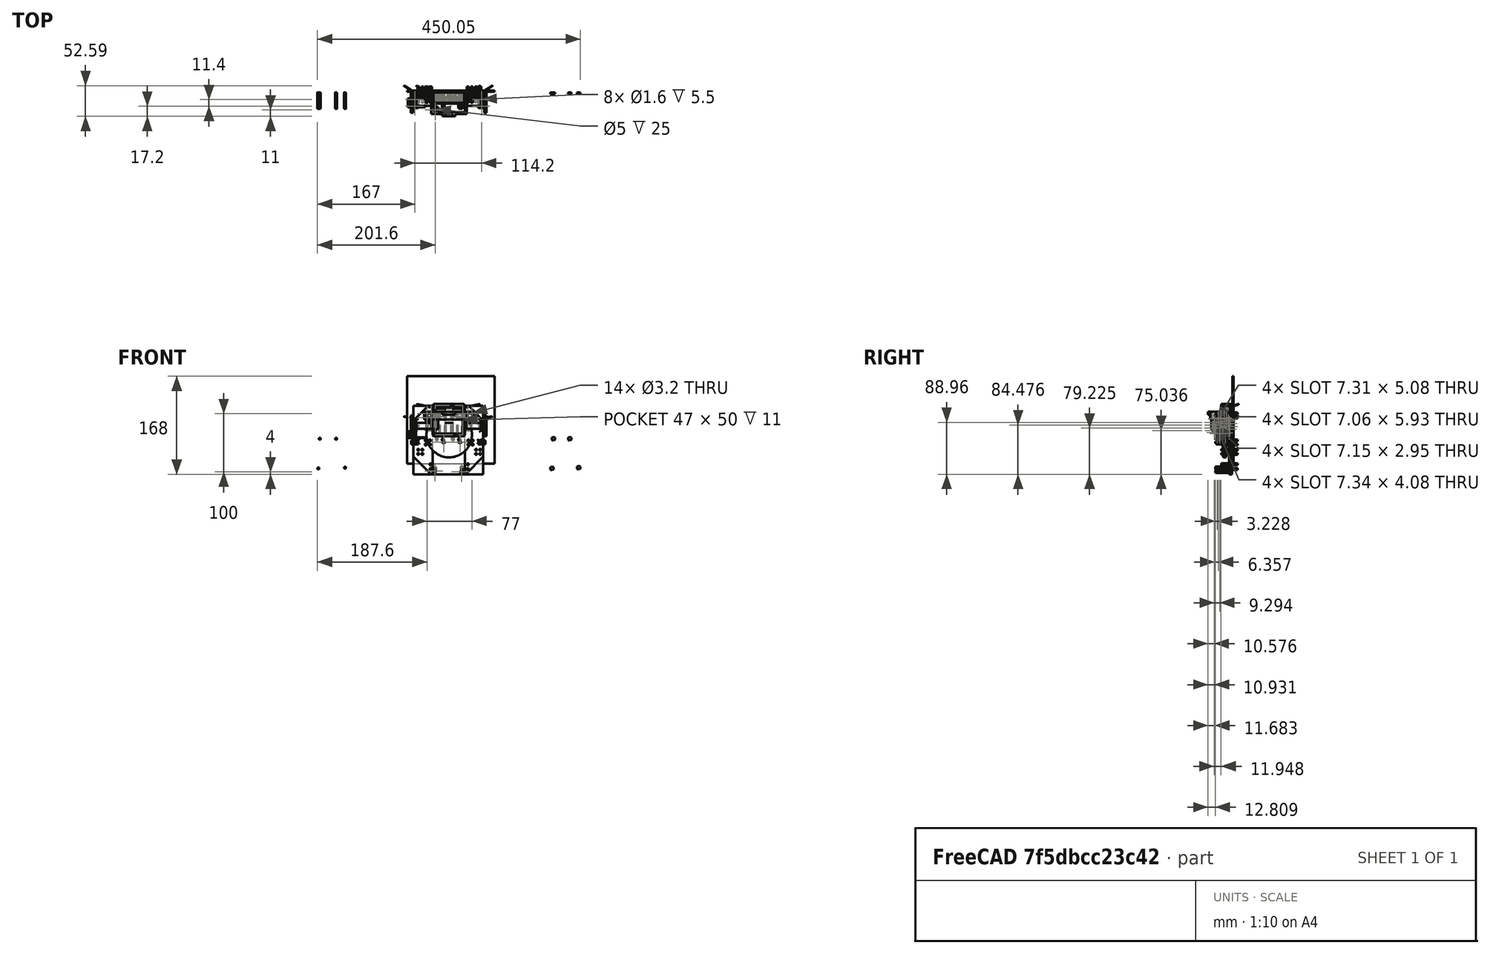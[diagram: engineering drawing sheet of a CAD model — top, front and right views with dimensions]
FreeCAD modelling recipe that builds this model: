
FCSTD DOCUMENT  (FreeCAD 0.16R6712 (Git))
Label: 5028.4 Blank Frank
License: All rights reserved
LicenseURL: http://en.wikipedia.org/wiki/All_rights_reserved
objects: Part::Cylinder×127, Part::Box×74, Part::Fuse×65, Part::Cut×64, Part::Feature×37, Part::MultiFuse×31, Part::Mirroring×14, Part::Fillet×10, Part::Chamfer×8, Part::Cone×8, Part::Compound×3, Part::Torus×2, App::DocumentObjectGroup×1
note: 443 computed .brp shape members not serialized (recipe doc carries the construction recipe); baked Part::Feature solids carry a one-line shape summary decoded from their .brp

FEATURE [Part::Cylinder] Cylinder
  Angle = 360
  Height = 30
  Radius = 7
FEATURE [Part::Cylinder] Cylinder001
  Angle = 360
  Height = 19
  Placement = pos=(0,0,30) rot=(0,0,1;0rad)
  Radius = 7
FEATURE [Part::Cylinder] Cylinder002
  Angle = 360
  Height = 1.8
  Placement = pos=(0,0,49) rot=(0,0,1;0rad)
  Radius = 2.5
FEATURE [Part::Compound] Compound
  Links = -> [Cylinder,Cylinder002,Cylinder001]
FEATURE [Part::Cylinder] Cylinder003
  Angle = 360
  Height = 30
  Radius = 7
FEATURE [Part::Cylinder] Cylinder004
  Angle = 360
  Height = 19
  Placement = pos=(0,0,30) rot=(0,0,1;0rad)
  Radius = 7
FEATURE [Part::Cylinder] Cylinder005
  Angle = 360
  Height = 1.8
  Placement = pos=(0,0,49) rot=(0,0,1;0rad)
  Radius = 2.5
FEATURE [Part::Compound] Compound001
  Links = -> [Cylinder003,Cylinder005,Cylinder004]
  Placement = pos=(14.5,0,50) rot=(1,0,0;3.14159rad)
FEATURE [Part::Cylinder] Cylinder006
  Angle = 360
  Height = 30
  Radius = 7
FEATURE [Part::Cylinder] Cylinder007
  Angle = 360
  Height = 19
  Placement = pos=(0,0,30) rot=(0,0,1;0rad)
  Radius = 7
FEATURE [Part::Cylinder] Cylinder008
  Angle = 360
  Height = 1.8
  Placement = pos=(0,0,49) rot=(0,0,1;0rad)
  Radius = 2.5
FEATURE [Part::Compound] Compound002
  Links = -> [Cylinder006,Cylinder008,Cylinder007]
  Placement = pos=(29,0,0) rot=(0,0,1;0rad)
FEATURE [Part::Box] Box  label="Cube"
  Height = 50
  Length = 47
  Placement = pos=(-9,-8,0) rot=(0,0,1;0rad)
  Width = 12
FEATURE [Part::Box] Box001  label="Cube001"
  Height = 55
  Length = 53
  Placement = pos=(-12,-8,-2.5) rot=(0,0,1;0rad)
  Width = 11
FEATURE [Part::Cylinder] Cylinder009
  Angle = 360
  Height = 50
  Radius = 7
FEATURE [Part::Cylinder] Cylinder010
  Angle = 360
  Height = 50
  Placement = pos=(14.5,0,0) rot=(0,0,1;0rad)
  Radius = 7
FEATURE [Part::Cut] Cut
  Base = -> Box001
  Tool = -> Box
FEATURE [Part::Box] Box002  label="Cube002"
  Height = 55
  Length = 53
  Placement = pos=(-12,3,-2.5) rot=(0,0,1;0rad)
  Width = 7
FEATURE [Part::Fuse] Fusion
  Base = -> Cut
  Tool = -> Box002
FEATURE [Part::Cut] Cut001  label="No idea why this is here...."
  Base = -> Fusion
  Tool = -> Cylinder009
FEATURE [Part::Cylinder] Cylinder011
  Angle = 360
  Height = 50
  Placement = pos=(29,0,0) rot=(0,0,1;0rad)
  Radius = 7
FEATURE [Part::Box] Box003  label="Cube003"
  Height = 5
  Length = 2
  Placement = pos=(28,-9,-2) rot=(0,0,1;0rad)
  Width = 12
FEATURE [Part::Box] Box004  label="Cube004"
  Height = 5
  Length = 2
  Placement = pos=(18.5,-9,46) rot=(0,0,1;0rad)
  Width = 12
FEATURE [Part::Box] Box005  label="Cube005"
  Height = 5
  Length = 2
  Placement = pos=(-2,-9,46) rot=(0,0,1;0rad)
  Width = 12
FEATURE [Part::Box] Box006  label="Cube006"
  Height = 5
  Length = 3
  Placement = pos=(35,-9,-4) rot=(0,0,1;0rad)
  Width = 12
FEATURE [Part::Cut] Cut008
FEATURE [Part::Torus] Torus001
  Angle1 = -180
  Angle2 = 180
  Angle3 = 360
  Placement = pos=(0,0,2) rot=(0,0,1;0rad)
  Radius1 = 19
  Radius2 = 1.5
FEATURE [Part::Cut] Cut009  label="wheel2"
  Base = -> Cut008
  Placement = pos=(75,-7,15) rot=(0,1,0;1.5708rad)
  Tool = -> Torus001
FEATURE [Part::Torus] Torus
  Angle1 = -180
  Angle2 = 180
  Angle3 = 360
  Placement = pos=(0,0,2) rot=(0,0,1;0rad)
  Radius1 = 19
  Radius2 = 1.5
FEATURE [Part::Cut] Cut010
FEATURE [Part::Cut] Cut011  label="wheel1"
  Base = -> Cut010
  Placement = pos=(-51,-7,15) rot=(0,1,0;1.5708rad)
  Tool = -> Torus
FEATURE [Part::Fuse] Fusion003
FEATURE [Part::Cylinder] Cylinder012
  Angle = 360
  Height = 10
  Placement = pos=(5,-4.5,0) rot=(0,1,0;1.5708rad)
  Radius = 0.8
FEATURE [Part::Fuse] Fusion048  label="right-motor001"
  Base = -> Cylinder012
  Placement = pos=(-51,-7,15) rot=(0,0,1;0rad)
  Tool = -> Fusion003
FEATURE [Part::Fuse] Fusion049
FEATURE [Part::Cylinder] Cylinder013
  Angle = 360
  Height = 10
  Placement = pos=(5,-4.5,0) rot=(0,1,0;1.5708rad)
  Radius = 0.8
FEATURE [Part::Fuse] Fusion050  label="left-motor001"
  Base = -> Cylinder013
  Placement = pos=(79,-7,15) rot=(0,0,1;3.14159rad)
  Tool = -> Fusion049
FEATURE [Part::Box] Box007  label="Cube007"
  Height = 5
  Length = 2
  Placement = pos=(37.5,-9,46) rot=(0,0,1;0rad)
  Width = 12
FEATURE [Part::Box] Box008  label="Cube008"
  Height = 5
  Length = 2
  Placement = pos=(8,-9,-2) rot=(0,0,1;0rad)
  Width = 12
FEATURE [Part::Box] Box009  label="The Ground"
  Height = 150
  Length = 150
  Placement = pos=(-57,11,-50) rot=(0,0,1;0rad)
  Width = 2
FEATURE [Part::Box] Box010  label="Motor Mount Left"
  Height = 16
  Length = 4
  Placement = pos=(69,-13,7) rot=(0,0,1;0rad)
  Width = 20
FEATURE [Part::Box] Box011  label="Motor Mount Right"
  Height = 16
  Length = 4
  Placement = pos=(-46,-13,7) rot=(0,0,1;0rad)
  Width = 20
FEATURE [Part::Box] Box012  label="Motor Support Right"
  Height = 16
  Length = 10
  Placement = pos=(-25,-1,7) rot=(0,0,1;0rad)
  Width = 8
FEATURE [Part::Box] Box013  label="Motor Support Left"
  Height = 16
  Length = 10
  Placement = pos=(43,-1,7) rot=(0,0,1;0rad)
  Width = 8
FEATURE [Part::Cylinder] Cylinder014
  Angle = 360
  Height = 28
  Placement = pos=(40.7,0,-10.3) rot=(1,0,0;1.5708rad)
  Radius = 1.6
FEATURE [Part::Cylinder] Cylinder015
  Angle = 360
  Height = 28
  Placement = pos=(-2.4,0,-59.8) rot=(1,0,0;1.5708rad)
  Radius = 1.6
FEATURE [Part::Cylinder] Cylinder016
  Angle = 360
  Height = 28
  Placement = pos=(-5,0,-9) rot=(1,0,0;1.5708rad)
  Radius = 1.6
FEATURE [Part::Cylinder] Cylinder017
  Angle = 360
  Height = 28
  Placement = pos=(25.5,0,-59.8) rot=(1,0,0;1.5708rad)
  Radius = 1.6
FEATURE [Part::Fuse] Fusion051
  Base = -> Cylinder015
  Tool = -> Cylinder016
FEATURE [Part::Fuse] Fusion052
  Base = -> Cylinder014
  Tool = -> Cylinder017
FEATURE [Part::Fuse] Fusion053  label="Screw holes on Arduino Duo"
  Base = -> Fusion051
  Tool = -> Fusion052
FEATURE [Part::Mirroring] Part__Mirroring  label="XXXXXScrew holes on Arduino Duo (Mirror #1)"
  Base = (0,0,0)
  Normal = (0,0,1)
  Placement = pos=(-204,10,-67) rot=(0,0,1;0rad)
  Source = -> Fusion053
FEATURE [Part::Box] Box014  label="Not used Cube"
  Height = 10
  Length = 10
  Placement = pos=(-1,4,-5.85) rot=(0,0,1;0rad)
  Width = 10
FEATURE [Part::Box] Box015  label="Cube014 Arduino Support cube"
  Height = 67
  Length = 55
  Placement = pos=(-13,5,-68) rot=(0,0,1;0rad)
  Width = 5
FEATURE [Part::Cylinder] Cylinder018
  Angle = 360
  Height = 5
  Placement = pos=(15,0,0) rot=(1,0,0;1.5708rad)
  Radius = 39
FEATURE [Part::Cut] Cut014  label="M3 Nut"
  Base = -> Cut001
  Placement = pos=(-6.4,10,-7.2) rot=(1,0,0;1.5708rad)
  Tool = -> Cylinder001
FEATURE [Part::Cut] Cut015  label="M3 Nut001"
  Base = -> Cut001
  Placement = pos=(21.5,10,-7.2) rot=(1,0,0;1.5708rad)
  Tool = -> Cylinder001
FEATURE [Part::Cut] Cut016  label="M3 Nut002"
  Base = -> Cut001
  Placement = pos=(36.7,10,-56.7) rot=(1,0,0;1.5708rad)
  Tool = -> Cylinder001
FEATURE [Part::Cut] Cut017  label="M3 Nut003"
  Base = -> Cut001
  Placement = pos=(-9,10,-58) rot=(1,0,0;1.5708rad)
  Tool = -> Cylinder001
FEATURE [Part::Cut] Cut018
  Base = -> Cut
  Placement = pos=(-9,10,-58) rot=(1,0,0;1.5708rad)
  Tool = -> Box006
FEATURE [Part::Cut] Cut019
  Base = -> Cut
  Placement = pos=(36.7,10,-56.7) rot=(1,0,0;1.5708rad)
  Tool = -> Box006
FEATURE [Part::Cut] Cut020
  Base = -> Cut
  Placement = pos=(-6.4,10,-7.2) rot=(1,0,0;1.5708rad)
  Tool = -> Box006
FEATURE [Part::Cut] Cut021
  Base = -> Cut
  Placement = pos=(21.5,10,-7.2) rot=(1,0,0;1.5708rad)
  Tool = -> Box006
FEATURE [Part::MultiFuse] Fusion054  label="XXXXXHex Holes"
  Placement = pos=(200,0,0) rot=(0,0,1;0rad)
  Shapes = -> [Cut018,Cut021,Cut019,Cut020]
FEATURE [Part::Box] Box016  label="Cube015"
  Height = 117
  Length = 33
  Placement = pos=(-46,7,-68) rot=(0,0,1;0rad)
  Width = 3
FEATURE [Part::Box] Box017  label="Cube016"
  Height = 117
  Length = 31
  Placement = pos=(42,7,-68) rot=(0,0,1;0rad)
  Width = 3
FEATURE [Part::Cylinder] Cylinder019
  Angle = 360
  Height = 28
  Placement = pos=(48,20,-10) rot=(1,0,0;1.5708rad)
  Radius = 1.6
FEATURE [Part::Cylinder] Cylinder020
  Angle = 360
  Height = 28
  Placement = pos=(47,20,-51) rot=(1,0,0;1.5708rad)
  Radius = 1.6
FEATURE [Part::Cylinder] Cylinder021
  Angle = 360
  Height = 28
  Placement = pos=(48,20,-17) rot=(1,0,0;1.5708rad)
  Radius = 1.6
FEATURE [Part::Cylinder] Cylinder022
  Angle = 360
  Height = 28
  Placement = pos=(47,20,-59) rot=(1,0,0;1.5708rad)
  Radius = 1.6
FEATURE [Part::Cylinder] Cylinder023
  Angle = 360
  Height = 28
  Placement = pos=(55,20,-17) rot=(1,0,0;1.5708rad)
  Radius = 1.6
FEATURE [Part::Cylinder] Cylinder024
  Angle = 360
  Height = 28
  Placement = pos=(55,20,-10) rot=(1,0,0;1.5708rad)
  Radius = 1.6
FEATURE [Part::MultiFuse] Fusion055
  Shapes = -> [Cylinder021,Cylinder023,Cylinder024,Cylinder019]
FEATURE [Part::MultiFuse] Fusion056
  Placement = pos=(13,0,-16) rot=(0,0,1;0rad)
  Shapes = -> [Cylinder021,Cylinder023,Cylinder024,Cylinder019]
FEATURE [Part::MultiFuse] Fusion057  label="Mount holes top left"
  Placement = pos=(-1,0,46) rot=(0,0,1;0rad)
  Shapes = -> [Cylinder021,Cylinder023,Cylinder024,Cylinder019]
FEATURE [Part::MultiFuse] Fusion058  label="Mount holes top right"
  Placement = pos=(-71,0,46) rot=(0,0,1;0rad)
  Shapes = -> [Cylinder021,Cylinder023,Cylinder024,Cylinder019]
FEATURE [Part::MultiFuse] Fusion059
  Shapes = -> [Cylinder022,Cylinder020,Fusion055,Fusion056]
FEATURE [Part::Mirroring] Part__Mirroring001  label="Mount holes bottom right"
  Base = (0,0,0)
  Normal = (1,0,0)
  Placement = pos=(30,0,0) rot=(0,0,1;0rad)
  Source = -> Fusion059
FEATURE [Part::Cylinder] Cylinder025
  Angle = 360
  Height = 28
  Placement = pos=(48,20,-10) rot=(1,0,0;1.5708rad)
  Radius = 1.6
FEATURE [Part::Cylinder] Cylinder026
  Angle = 360
  Height = 28
  Placement = pos=(47,20,-51) rot=(1,0,0;1.5708rad)
  Radius = 1.6
FEATURE [Part::Cylinder] Cylinder027
  Angle = 360
  Height = 28
  Placement = pos=(48,20,-17) rot=(1,0,0;1.5708rad)
  Radius = 1.6
FEATURE [Part::Cylinder] Cylinder028
  Angle = 360
  Height = 28
  Placement = pos=(47,20,-59) rot=(1,0,0;1.5708rad)
  Radius = 1.6
FEATURE [Part::Cylinder] Cylinder029
  Angle = 360
  Height = 28
  Placement = pos=(55,20,-17) rot=(1,0,0;1.5708rad)
  Radius = 1.6
FEATURE [Part::Cylinder] Cylinder030
  Angle = 360
  Height = 28
  Placement = pos=(55,20,-10) rot=(1,0,0;1.5708rad)
  Radius = 1.6
FEATURE [Part::MultiFuse] Fusion060
  Shapes = -> [Cylinder027,Cylinder029,Cylinder030,Cylinder025]
FEATURE [Part::MultiFuse] Fusion061
  Placement = pos=(13,0,-16) rot=(0,0,1;0rad)
  Shapes = -> [Cylinder027,Cylinder029,Cylinder030,Cylinder025]
FEATURE [Part::MultiFuse] Fusion062  label="Mount holes bottom left"
  Shapes = -> [Cylinder028,Cylinder026,Fusion060,Fusion061]
FEATURE [Part::Cylinder] Cylinder031  label="Cylinder123"
  Angle = 360
  Height = 10
  Placement = pos=(0,18,29) rot=(0,0,1;0rad)
  Radius = 2.25
FEATURE [Part::Cylinder] Cylinder032  label="Cylinder124"
  Angle = 360
  Height = 10
  Placement = pos=(4.5,18,32) rot=(0,0,1;0rad)
  Radius = 1
FEATURE [Part::Cylinder] Cylinder033  label="Cylinder125"
  Angle = 360
  Height = 10
  Placement = pos=(-4.5,18,32) rot=(0,0,1;0rad)
  Radius = 1
FEATURE [Part::Fuse] Fusion009  label="Mounting Screw Holes"
  Base = -> Cylinder032
  Tool = -> Cylinder033
FEATURE [Part::Fuse] Fusion071  label="Motor Holes Left"
  Base = -> Cylinder031
  Placement = pos=(37,-7,-3) rot=(0.57735,0.57735,0.57735;2.0944rad)
  Tool = -> Fusion009
FEATURE [Part::Cylinder] Cylinder034  label="Cylinder126"
  Angle = 360
  Height = 10
  Placement = pos=(0,18,29) rot=(0,0,1;0rad)
  Radius = 2.25
FEATURE [Part::Cylinder] Cylinder035  label="Cylinder127"
  Angle = 360
  Height = 10
  Placement = pos=(4.5,18,32) rot=(0,0,1;0rad)
  Radius = 1
FEATURE [Part::Cylinder] Cylinder036  label="Cylinder128"
  Angle = 360
  Height = 10
  Placement = pos=(-4.5,18,32) rot=(0,0,1;0rad)
  Radius = 1
FEATURE [Part::Fuse] Fusion072  label="Mounting Screw Holes001"
  Base = -> Cylinder035
  Tool = -> Cylinder036
FEATURE [Part::Fuse] Fusion073  label="Motor Holes Right"
  Base = -> Cylinder034
  Placement = pos=(-79,-7,-3) rot=(0.57735,0.57735,0.57735;2.0944rad)
  Tool = -> Fusion072
FEATURE [Part::Cylinder] Cylinder037  label="Cylinder129"
  Angle = 360
  Height = 28
  Placement = pos=(40.7,0,-10.3) rot=(1,0,0;1.5708rad)
  Radius = 1.6
FEATURE [Part::Cylinder] Cylinder038  label="Cylinder130"
  Angle = 360
  Height = 28
  Placement = pos=(-2.4,0,-59.8) rot=(1,0,0;1.5708rad)
  Radius = 1.6
FEATURE [Part::Cylinder] Cylinder039  label="Cylinder131"
  Angle = 360
  Height = 28
  Placement = pos=(-5,0,-9) rot=(1,0,0;1.5708rad)
  Radius = 1.6
FEATURE [Part::Cylinder] Cylinder040  label="Cylinder132"
  Angle = 360
  Height = 28
  Placement = pos=(25.5,0,-59.8) rot=(1,0,0;1.5708rad)
  Radius = 1.6
FEATURE [Part::Fuse] Fusion074
  Base = -> Cylinder038
  Tool = -> Cylinder039
FEATURE [Part::Fuse] Fusion075
  Base = -> Cylinder037
  Tool = -> Cylinder040
FEATURE [Part::Fuse] Fusion076  label="Screw holes on Arduino Duo001"
  Base = -> Fusion074
  Tool = -> Fusion075
FEATURE [Part::Mirroring] Part__Mirroring002  label="Screw holes on Arduino Duo (Mirror #1)001"
  Base = (0,0,0)
  Normal = (0,0,1)
  Placement = pos=(-4,10,-67) rot=(0,0,1;0rad)
  Source = -> Fusion076
FEATURE [Part::Mirroring] Part__Mirroring003  label="Screw holes on Arduino Duo (Mirror #1)001 (Mirror #4)"
  Base = (0,0,0)
  Normal = (1,0,0)
  Placement = pos=(27,0,-6) rot=(0,0,1;0rad)
  Source = -> Part__Mirroring002
FEATURE [Part::Box] Box018  label="Cube017"
  Height = 50
  Length = 47
  Placement = pos=(-9,-8,0) rot=(0,0,1;0rad)
  Width = 12
FEATURE [Part::Box] Box019  label="Cube018"
  Height = 55
  Length = 53
  Placement = pos=(-12,-8,-2.5) rot=(0,0,1;0rad)
  Width = 11
FEATURE [Part::Cut] Cut031
  Base = -> Box019
  Tool = -> Box018
FEATURE [Part::Box] Box020  label="Cube019"
  Height = 5
  Length = 3
  Placement = pos=(35,-9,-4) rot=(0,0,1;0rad)
  Width = 12
FEATURE [Part::Cut] Cut032
  Base = -> Cut031
  Placement = pos=(-9,10,-58) rot=(1,0,0;1.5708rad)
  Tool = -> Box020
FEATURE [Part::Cut] Cut033
  Base = -> Cut031
  Placement = pos=(36.7,10,-56.7) rot=(1,0,0;1.5708rad)
  Tool = -> Box020
FEATURE [Part::Cut] Cut034
  Base = -> Cut031
  Placement = pos=(-6.4,10,-7.2) rot=(1,0,0;1.5708rad)
  Tool = -> Box020
FEATURE [Part::Cut] Cut035
  Base = -> Cut031
  Placement = pos=(21.5,10,-7.2) rot=(1,0,0;1.5708rad)
  Tool = -> Box020
FEATURE [Part::MultiFuse] Fusion077
  Shapes = -> [Cut032,Cut035,Cut033,Cut034]
FEATURE [Part::Mirroring] Part__Mirroring004  label="Hex Holes"
  Base = (0,0,0)
  Normal = (1,0,0)
  Placement = pos=(27,0,-6) rot=(0,0,1;0rad)
  Source = -> Fusion077
FEATURE [Part::Box] Box021  label="Cube020"
  Height = 13
  Length = 61
  Placement = pos=(-16,-27,26) rot=(0,0,1;0rad)
  Width = 34
FEATURE [Part::Box] Box022  label="Cube021"
  Height = 13
  Length = 12
  Placement = pos=(45,4,26) rot=(0,0,1;0rad)
  Width = 3
FEATURE [Part::Box] Box023  label="Cube022"
  Height = 13
  Length = 12
  Placement = pos=(-28,4,26) rot=(0,0,1;0rad)
  Width = 3
FEATURE [Part::Box] Box024  label="Cube023"
  Height = 13
  Length = 55
  Placement = pos=(-13,-24,26) rot=(0,0,1;0rad)
  Width = 31
FEATURE [Part::Cylinder] Cylinder041  label="Cylinder133"
  Angle = 360
  Height = 28
  Placement = pos=(54,20,29) rot=(1,0,0;1.5708rad)
  Radius = 1.6
FEATURE [Part::Cylinder] Cylinder042  label="Cylinder134"
  Angle = 360
  Height = 28
  Placement = pos=(54,20,36) rot=(1,0,0;1.5708rad)
  Radius = 1.6
FEATURE [Part::Cylinder] Cylinder043  label="Cylinder135"
  Angle = 360
  Height = 28
  Placement = pos=(-23,20,29) rot=(1,0,0;1.5708rad)
  Radius = 1.6
FEATURE [Part::Cylinder] Cylinder044  label="Cylinder136"
  Angle = 360
  Height = 28
  Placement = pos=(-23,20,36) rot=(1,0,0;1.5708rad)
  Radius = 1.6
FEATURE [Part::Cylinder] Cylinder045  label="Cylinder137"
  Angle = 360
  Height = 10
  Placement = pos=(36,-17.25,32.5) rot=(0,1,0;1.5708rad)
  Radius = 2.5
FEATURE [Part::Cut] Cut037
  Base = -> Box021
  Tool = -> Box024
FEATURE [Part::Cut] Cut038
  Base = -> Cut037
  Tool = -> Cylinder045
FEATURE [Part::Box] Box025  label="Cube024"
  Height = 5
  Length = 22
  Placement = pos=(3.5,-31,34) rot=(0,0,1;0rad)
  Width = 4
FEATURE [Part::Cylinder] Cylinder046  label="Cylinder138"
  Angle = 360
  Height = 10
  Placement = pos=(20.75,-29,30) rot=(0,0,1;0rad)
  Radius = 0.85
FEATURE [Part::Cylinder] Cylinder047  label="Cylinder139"
  Angle = 360
  Height = 10
  Placement = pos=(8.25,-29,40) rot=(1,0,0;3.14159rad)
  Radius = 0.85
FEATURE [Part::Fuse] Fusion078
  Base = -> Cylinder046
  Tool = -> Cylinder047
FEATURE [Part::Cut] Cut039
  Base = -> Box025
  Tool = -> Fusion078
FEATURE [Part::Fuse] Fusion079
  Base = -> Cut038
  Tool = -> Cut039
FEATURE [Part::Fuse] Fusion080
  Base = -> Cylinder043
  Tool = -> Cylinder044
FEATURE [Part::Fuse] Fusion081
  Base = -> Cylinder041
  Tool = -> Cylinder042
FEATURE [Part::Fuse] Fusion082
  Base = -> Box023
  Tool = -> Fusion079
FEATURE [Part::Fuse] Fusion083
  Base = -> Box022
  Tool = -> Fusion082
FEATURE [Part::Cut] Cut040
  Base = -> Fusion083
  Tool = -> Fusion081
FEATURE [Part::Cut] Cut041  label="Switch Bracket"
  Base = -> Cut040
  Tool = -> Fusion080
FEATURE [Part::Cylinder] Cylinder048  label="Cylinder140"
  Angle = 360
  Height = 28
  Placement = pos=(-23,20,29) rot=(1,0,0;1.5708rad)
  Radius = 1.6
FEATURE [Part::Cylinder] Cylinder049  label="Cylinder141"
  Angle = 360
  Height = 28
  Placement = pos=(-23,20,36) rot=(1,0,0;1.5708rad)
  Radius = 1.6
FEATURE [Part::Fuse] Fusion084
  Base = -> Cylinder048
  Placement = pos=(1,0,0) rot=(0,0,1;0rad)
  Tool = -> Cylinder049
FEATURE [Part::Cylinder] Cylinder050  label="Cylinder142"
  Angle = 360
  Height = 28
  Placement = pos=(-23,20,29) rot=(1,0,0;1.5708rad)
  Radius = 1.6
FEATURE [Part::Cylinder] Cylinder051  label="Cylinder143"
  Angle = 360
  Height = 28
  Placement = pos=(-23,20,36) rot=(1,0,0;1.5708rad)
  Radius = 1.6
FEATURE [Part::Fuse] Fusion085
  Base = -> Cylinder050
  Placement = pos=(-1,0,0) rot=(0,0,1;0rad)
  Tool = -> Cylinder051
FEATURE [Part::Cut] Cut042
  Base = -> Cut041
  Tool = -> Fusion084
FEATURE [Part::Cut] Cut043  label="Switch Bracket001"
  Base = -> Cut042
  Tool = -> Fusion085
FEATURE [Part::Cylinder] Cylinder052  label="Cylinder144"
  Angle = 360
  Height = 42
  Radius = 4.8
FEATURE [Part::Cylinder] Cylinder053  label="Cylinder145"
  Angle = 360
  Height = 1.6
  Placement = pos=(0,0,42) rot=(0,0,1;0rad)
  Radius = 1.65
FEATURE [Part::Fuse] Fusion086
  Base = -> Cylinder052
  Placement = pos=(2,0,0) rot=(0,0,1;0rad)
  Tool = -> Cylinder053
FEATURE [Part::Cylinder] Cylinder054  label="Cylinder146"
  Angle = 360
  Height = 42
  Radius = 4.8
FEATURE [Part::Cylinder] Cylinder055  label="Cylinder147"
  Angle = 360
  Height = 1.6
  Placement = pos=(0,0,42) rot=(0,0,1;0rad)
  Radius = 1.65
FEATURE [Part::Fuse] Fusion087
  Base = -> Cylinder054
  Placement = pos=(12,0,0) rot=(0,0,1;0rad)
  Tool = -> Cylinder055
FEATURE [Part::Cylinder] Cylinder056  label="Cylinder148"
  Angle = 360
  Height = 42
  Radius = 4.8
FEATURE [Part::Cylinder] Cylinder057  label="Cylinder149"
  Angle = 360
  Height = 1.6
  Placement = pos=(0,0,42) rot=(0,0,1;0rad)
  Radius = 1.65
FEATURE [Part::Fuse] Fusion088
  Base = -> Cylinder056
  Placement = pos=(22,0,0) rot=(0,0,1;0rad)
  Tool = -> Cylinder057
FEATURE [Part::Cylinder] Cylinder058  label="Cylinder150"
  Angle = 360
  Height = 42
  Radius = 4.8
FEATURE [Part::Cylinder] Cylinder059  label="Cylinder151"
  Angle = 360
  Height = 1.6
  Placement = pos=(0,0,42) rot=(0,0,1;0rad)
  Radius = 1.65
FEATURE [Part::Fuse] Fusion089
  Base = -> Cylinder058
  Placement = pos=(32,0,0) rot=(0,0,1;0rad)
  Tool = -> Cylinder059
FEATURE [Part::Cylinder] Cylinder060  label="Cylinder152"
  Angle = 360
  Height = 42
  Radius = 4.8
FEATURE [Part::Cylinder] Cylinder061  label="Cylinder153"
  Angle = 360
  Height = 1.6
  Placement = pos=(0,0,42) rot=(0,0,1;0rad)
  Radius = 1.65
FEATURE [Part::Fuse] Fusion093
  Base = -> Cylinder060
  Placement = pos=(-8,0,0) rot=(0,0,1;0rad)
  Tool = -> Cylinder061
FEATURE [Part::MultiFuse] Fusion094  label="AAA Batts"
  Placement = pos=(2.5,0,2) rot=(0,0,1;0rad)
  Shapes = -> [Fusion093,Fusion086,Fusion087,Fusion088,Fusion089]
FEATURE [Part::Cylinder] Cylinder062  label="Cylinder154"
  Angle = 360
  Height = 10
  Radius = 17
FEATURE [Part::Cylinder] Cylinder063  label="Cylinder155"
  Angle = 360
  Height = 16
  Placement = pos=(0,0,-4) rot=(0,0,1;0rad)
  Radius = 10
FEATURE [Part::Cut] Cut044
  Base = -> Cylinder062
  Tool = -> Cylinder063
FEATURE [Part::Box] Box026  label="Cube025"
  Height = 20
  Length = 18
  Placement = pos=(0,0,-5) rot=(0,0,1;0rad)
  Width = 20
FEATURE [Part::Box] Box027  label="Cube026"
  Height = 20
  Length = 10
  Placement = pos=(0,0,-5) rot=(0,0,1;0.174533rad)
  Width = 20
FEATURE [Part::Cut] Cut045
  Base = -> Box027
  Tool = -> Box026
FEATURE [Part::Feature] Cut045001
  Placement = pos=(0,0,0) rot=(0,0,1;0.349066rad)
  shape: bbox 10 x 22.32 x 20 mm, 7 faces (baked)
FEATURE [Part::Feature] Cut045002
  Placement = pos=(0,0,0) rot=(0,0,1;0.698132rad)
  shape: bbox 15.32 x 20.52 x 20 mm, 7 faces (baked)
FEATURE [Part::Feature] Cut045003
  Placement = pos=(0,0,0) rot=(0,0,1;1.0472rad)
  shape: bbox 18.79 x 16.24 x 20 mm, 7 faces (baked)
FEATURE [Part::Feature] Cut045004
  Placement = pos=(0,0,0) rot=(0,0,1;1.39626rad)
  shape: bbox 20 x 10 x 20 mm, 7 faces (baked)
FEATURE [Part::Feature] Cut045005
  Placement = pos=(0,0,0) rot=(0,0,1;1.74533rad)
  shape: bbox 22.21 x 9.894 x 20 mm, 7 faces (baked)
FEATURE [Part::Feature] Cut045006
  Placement = pos=(0,0,0) rot=(0,0,1;2.0944rad)
  shape: bbox 21.75 x 12.86 x 20 mm, 7 faces (baked)
FEATURE [Part::Feature] Cut045007
  Placement = pos=(0,0,0) rot=(0,0,1;2.44346rad)
  shape: bbox 18.66 x 17.32 x 20 mm, 7 faces (baked)
FEATURE [Part::Feature] Cut045008
  Placement = pos=(0,0,0) rot=(0,0,1;2.79253rad)
  shape: bbox 13.32 x 19.7 x 20 mm, 7 faces (baked)
FEATURE [Part::Feature] Cut045009
  Placement = pos=(0,0,0) rot=(0,0,1;3.14159rad)
  shape: bbox 10.1 x 21.43 x 20 mm, 7 faces (baked)
FEATURE [Part::Feature] Cut045010
  Placement = pos=(0,0,0) rot=(0,0,1;3.49066rad)
  shape: bbox 10 x 22.32 x 20 mm, 7 faces (baked)
FEATURE [Part::Feature] Cut045011
  Placement = pos=(0,0,0) rot=(0,0,1;3.83972rad)
  shape: bbox 15.32 x 20.52 x 20 mm, 7 faces (baked)
FEATURE [Part::Feature] Cut045012
  Placement = pos=(0,0,0) rot=(0,0,1;4.18879rad)
  shape: bbox 18.79 x 16.24 x 20 mm, 7 faces (baked)
FEATURE [Part::Feature] Cut045013
  Placement = pos=(0,0,0) rot=(0,0,-1;1.74533rad)
  shape: bbox 20 x 10 x 20 mm, 7 faces (baked)
FEATURE [Part::Feature] Cut045014
  Placement = pos=(0,0,0) rot=(0,0,-1;1.39626rad)
  shape: bbox 22.21 x 9.894 x 20 mm, 7 faces (baked)
FEATURE [Part::Feature] Cut045015
  Placement = pos=(0,0,0) rot=(0,0,-1;1.0472rad)
  shape: bbox 21.75 x 12.86 x 20 mm, 7 faces (baked)
FEATURE [Part::Feature] Cut045016
  Placement = pos=(0,0,0) rot=(0,0,-1;0.698132rad)
  shape: bbox 18.66 x 17.32 x 20 mm, 7 faces (baked)
FEATURE [Part::Feature] Cut045017
  Placement = pos=(0,0,0) rot=(0,0,-1;0.349066rad)
  shape: bbox 13.32 x 19.7 x 20 mm, 7 faces (baked)
FEATURE [Part::MultiFuse] Fusion095
  Shapes = -> [Cut045001,Cut045008,Cut045010,Cut045009,Cut045005,Cut045003,Cut045006,Cut045002,Cut045004,Cut045007,Cut045016,Cut045017,Cut045011,Cut045012,Cut045013,Cut045014,Cut045015,Cut045]
FEATURE [Part::Cut] Cut045018
  Base = -> Cut044
  Placement = pos=(72,-7,15) rot=(0,1,0;1.5708rad)
  Tool = -> Fusion095
FEATURE [Part::Cut] Cut045019  label="Wheel with Spokes AB"
  Base = -> Cut009
  Tool = -> Cut045018
FEATURE [Part::Box] Box028  label="Cube027"
  Height = 5
  Length = 2
  Placement = pos=(37.5,-9,-2) rot=(0,0,1;0rad)
  Width = 12
FEATURE [Part::Box] Box029  label="Cube028"
  Height = 50
  Length = 47
  Placement = pos=(-9,-8,0) rot=(0,0,1;0rad)
  Width = 12
FEATURE [Part::Box] Box030  label="Cube029"
  Height = 55
  Length = 53
  Placement = pos=(-12,-8,-2.5) rot=(0,0,1;0rad)
  Width = 11
FEATURE [Part::Cylinder] Cylinder064  label="Cylinder156"
  Angle = 360
  Height = 50
  Radius = 7
FEATURE [Part::Cut] Cut045020
  Base = -> Box030
  Tool = -> Box029
FEATURE [Part::Box] Box031  label="Cube030"
  Height = 55
  Length = 53
  Placement = pos=(-12,3,-2.5) rot=(0,0,1;0rad)
  Width = 7
FEATURE [Part::Fuse] Fusion096
  Base = -> Cut045020
  Tool = -> Box031
FEATURE [App::DocumentObjectGroup] Group  label="Older version parts"
  Group = -> [Compound,Compound001,Compound002,Cylinder064,Cylinder010,Cylinder011,Fusion096,Part__Mirroring,Fusion054,Part__Mirroring004,Cut014,Cut015,Cut016,Cut017]
FEATURE [Part::Box] Box032  label="Battery Base"
  Height = 50
  Length = 55
  Placement = pos=(-13,3,-1) rot=(0,0,1;0rad)
  Width = 7
FEATURE [Part::Box] Box033  label="Cube031"
  Height = 30
  Length = 10
  Placement = pos=(-14,-25,9) rot=(0,0,1;0rad)
  Width = 10
FEATURE [Part::Cylinder] Cylinder065  label="Cylinder157"
  Angle = 360
  Height = 43.5
  Placement = pos=(4,0,2) rot=(0,0,1;0rad)
  Radius = 4.8
FEATURE [Part::Cylinder] Cylinder066  label="Cylinder158"
  Angle = 360
  Height = 1.6
  Placement = pos=(4,0,44) rot=(0,0,1;0rad)
  Radius = 1.65
FEATURE [Part::Fuse] Fusion097
  Base = -> Cylinder065
  Tool = -> Cylinder066
FEATURE [Part::Cylinder] Cylinder067  label="Cylinder159"
  Angle = 360
  Height = 43.5
  Placement = pos=(14,0,2) rot=(0,0,1;0rad)
  Radius = 4.8
FEATURE [Part::Cylinder] Cylinder068  label="Cylinder160"
  Angle = 360
  Height = 1.6
  Placement = pos=(14,0,44) rot=(0,0,1;0rad)
  Radius = 1.65
FEATURE [Part::Fuse] Fusion098
  Base = -> Cylinder067
  Tool = -> Cylinder068
FEATURE [Part::Cylinder] Cylinder069  label="Cylinder161"
  Angle = 360
  Height = 43.5
  Placement = pos=(24,0,2) rot=(0,0,1;0rad)
  Radius = 4.8
FEATURE [Part::Cylinder] Cylinder070  label="Cylinder162"
  Angle = 360
  Height = 1.6
  Placement = pos=(24,0,44) rot=(0,0,1;0rad)
  Radius = 1.65
FEATURE [Part::Fuse] Fusion099
  Base = -> Cylinder069
  Tool = -> Cylinder070
FEATURE [Part::Cylinder] Cylinder071  label="Cylinder163"
  Angle = 360
  Height = 43.5
  Placement = pos=(34,0,2) rot=(0,0,1;0rad)
  Radius = 4.8
FEATURE [Part::Cylinder] Cylinder072  label="Cylinder164"
  Angle = 360
  Height = 1.6
  Placement = pos=(34,0,44) rot=(0,0,1;0rad)
  Radius = 1.65
FEATURE [Part::Fuse] Fusion100
  Base = -> Cylinder071
  Tool = -> Cylinder072
FEATURE [Part::Cylinder] Cylinder073  label="Cylinder165"
  Angle = 360
  Height = 43.5
  Placement = pos=(-6,0,2) rot=(0,0,1;0rad)
  Radius = 4.8
FEATURE [Part::Cylinder] Cylinder074  label="Cylinder166"
  Angle = 360
  Height = 1.6
  Placement = pos=(-6,0,44) rot=(0,0,1;0rad)
  Radius = 1.65
FEATURE [Part::Fuse] Fusion101
  Base = -> Cylinder073
  Tool = -> Cylinder074
FEATURE [Part::MultiFuse] Fusion102  label="AAA Batts001"
  Shapes = -> [Fusion101,Fusion097,Fusion098,Fusion099,Fusion100]
FEATURE [Part::Cylinder] Cylinder075  label="Cylinder167"
  Angle = 360
  Height = 10
  Placement = pos=(-9,-20,4) rot=(0,0,1;0rad)
  Radius = 2.75
FEATURE [Part::Cylinder] Cylinder076  label="Cylinder168"
  Angle = 360
  Height = 27
  Placement = pos=(-9,-20,14) rot=(0,0,1;0rad)
  Radius = 2.5
FEATURE [Part::Fuse] Fusion103  label="phototransistor hole"
  Base = -> Cylinder075
  Tool = -> Cylinder076
FEATURE [Part::Cut] Cut045021  label="Phototransistor holder"
  Base = -> Box033
  Tool = -> Fusion103
FEATURE [Part::Fuse] Fusion104  label="Switch Mount with phototransistor hole"
  Base = -> Cut043
  Tool = -> Cut045021
FEATURE [Part::Cut] Cut045022
  Base = -> Box032
  Tool = -> Fusion102
FEATURE [Part::Box] Box034  label="Cube032"
  Height = 2.5
  Length = 55
  Placement = pos=(-13,-9,-1) rot=(0,0,1;0rad)
  Width = 12
FEATURE [Part::Box] Box035  label="Cube033"
  Height = 2.5
  Length = 55
  Placement = pos=(-13,-9,46.5) rot=(0,0,1;0rad)
  Width = 12
FEATURE [Part::Box] Box036  label="Cube034"
  Height = 50
  Length = 2.5
  Placement = pos=(-13,-9,-1) rot=(0,0,1;0rad)
  Width = 12
FEATURE [Part::Box] Box037  label="Cube035"
  Height = 50
  Length = 2.5
  Placement = pos=(39.5,-9,-1) rot=(0,0,1;0rad)
  Width = 12
FEATURE [Part::MultiFuse] Fusion105
  Shapes = -> [Box034,Box036,Box037,Box035]
FEATURE [Part::Box] Box038  label="Cube036"
  Height = 5
  Length = 2
  Placement = pos=(-10.5,-9,46) rot=(0,0,1;0rad)
  Width = 12
FEATURE [Part::Box] Box039  label="Cube037"
  Height = 5
  Length = 2
  Placement = pos=(-10.5,-9,-2) rot=(0,0,1;0rad)
  Width = 12
FEATURE [Part::MultiFuse] Fusion106
  Shapes = -> [Box039,Box038,Box028,Box007]
FEATURE [Part::MultiFuse] Fusion107
  Shapes = -> [Box003,Box004,Box005,Box008]
FEATURE [Part::Cut] Cut045023
  Base = -> Fusion105
  Tool = -> Fusion106
FEATURE [Part::Cut] Cut045024
  Base = -> Cut045023
  Tool = -> Fusion107
FEATURE [Part::Box] Box040  label="Cube038"
  Height = 1.6
  Length = 30
  Placement = pos=(-56,-15.5,-6) rot=(0,0,1;0rad)
  Width = 15
FEATURE [Part::Box] Box041  label="Cube039"
  Height = 10
  Length = 14
  Placement = pos=(-56,-10.5,-4.5) rot=(0,0,1;0rad)
  Width = 6
FEATURE [Part::Box] Box042  label="Cube040"
  Height = 10
  Length = 5.3
  Placement = pos=(-51.7,-11.5,-4.5) rot=(0,0,1;0rad)
  Width = 8
FEATURE [Part::Cut] Cut045025
  Base = -> Box041
  Tool = -> Box042
FEATURE [Part::Fuse] Fusion108  label="Spoke Sensor PCB"
  Base = -> Box040
  Tool = -> Cut045025
FEATURE [Part::Cylinder] Cylinder077  label="Cylinder169"
  Angle = 360
  Height = 14.5
  Placement = pos=(-43.6,-2.4,-9) rot=(0,0,1;0rad)
  Radius = 0.8
FEATURE [Part::Cylinder] Cylinder078  label="Cylinder170"
  Angle = 360
  Height = 14.5
  Placement = pos=(-43.6,-13.8,-9) rot=(0,0,1;0rad)
  Radius = 0.8
FEATURE [Part::Fuse] Fusion109
  Base = -> Cylinder077
  Tool = -> Cylinder078
FEATURE [Part::Cut] Cut045026  label="Spoke Sensor PCB001"
  Base = -> Fusion108
  Tool = -> Fusion109
FEATURE [Part::Cylinder] Cylinder079  label="Cylinder171"
  Angle = 360
  Height = 14.5
  Placement = pos=(-43.6,-2.4,-18) rot=(0,0,1;0rad)
  Radius = 0.8
FEATURE [Part::Cylinder] Cylinder080  label="Cylinder172"
  Angle = 360
  Height = 14.5
  Placement = pos=(-43.6,-13.8,-18) rot=(0,0,1;0rad)
  Radius = 0.8
FEATURE [Part::Fuse] Fusion110  label="Batt Holder"
  Base = -> Cut045022
  Tool = -> Cut045024
FEATURE [Part::Box] Box043  label="Cube041"
  Height = 4
  Length = 12
  Placement = pos=(-50,-16.75,-17) rot=(0,0,1;0rad)
  Width = 26.75
FEATURE [Part::Chamfer] Chamfer
  Base = -> Box043
  Edges = 1 edges r=7: [Edge3]
FEATURE [Part::Cone] Cone
  Angle = 360
  Height = 1.5
  Placement = pos=(-43.6,-2.4,-13) rot=(0,0,1;0rad)
  Radius1 = 2.75
  Radius2 = 1.25
FEATURE [Part::Cone] Cone001
  Angle = 360
  Height = 1.5
  Placement = pos=(-43.6,-13.8,-13) rot=(0,0,1;0rad)
  Radius1 = 2.75
  Radius2 = 1.25
FEATURE [Part::Fuse] Fusion111
  Base = -> Cone
  Tool = -> Cone001
FEATURE [Part::Fuse] Fusion112
  Base = -> Chamfer
  Tool = -> Fusion111
FEATURE [Part::Fuse] Fusion113
  Base = -> Cylinder079
  Tool = -> Cylinder080
FEATURE [Part::Cut] Cut045027
  Base = -> Fusion112
  Tool = -> Fusion113
FEATURE [Part::Cylinder] Cylinder081  label="Cylinder173"
  Angle = 360
  Height = 14.5
  Placement = pos=(-43.6,-2.4,-18) rot=(0,0,1;0rad)
  Radius = 0.8
FEATURE [Part::Cylinder] Cylinder082  label="Cylinder174"
  Angle = 360
  Height = 14.5
  Placement = pos=(-43.6,-13.8,-18) rot=(0,0,1;0rad)
  Radius = 0.8
FEATURE [Part::Box] Box044  label="Cube042"
  Height = 4
  Length = 12
  Placement = pos=(-50,-16.75,-17) rot=(0,0,1;0rad)
  Width = 26.75
FEATURE [Part::Chamfer] Chamfer001
  Base = -> Box044
  Edges = 1 edges r=7: [Edge3]
FEATURE [Part::Cone] Cone002
  Angle = 360
  Height = 1.5
  Placement = pos=(-43.6,-2.4,-13) rot=(0,0,1;0rad)
  Radius1 = 2.75
  Radius2 = 1.25
FEATURE [Part::Cone] Cone003
  Angle = 360
  Height = 1.5
  Placement = pos=(-43.6,-13.8,-13) rot=(0,0,1;0rad)
  Radius1 = 2.75
  Radius2 = 1.25
FEATURE [Part::Fuse] Fusion114
  Base = -> Cone002
  Tool = -> Cone003
FEATURE [Part::Fuse] Fusion115
  Base = -> Chamfer001
  Tool = -> Fusion114
FEATURE [Part::Fuse] Fusion116
  Base = -> Cylinder081
  Tool = -> Cylinder082
FEATURE [Part::Cut] Cut045028
  Base = -> Fusion115
  Tool = -> Fusion116
FEATURE [Part::Mirroring] Part__Mirroring005  label="Cut045028 (Mirror #6)"
  Base = (0,0,0)
  Normal = (1,0,0)
  Placement = pos=(27,0,0) rot=(0,0,1;0rad)
  Source = -> Cut045028
FEATURE [Part::Box] Box045  label="Cube043"
  Height = 5
  Length = 2
  Placement = pos=(28,-9,-2) rot=(0,0,1;0rad)
  Width = 12
FEATURE [Part::Box] Box046  label="Cube044"
  Height = 5
  Length = 2
  Placement = pos=(18.5,-9,46) rot=(0,0,1;0rad)
  Width = 12
FEATURE [Part::Box] Box047  label="Cube045"
  Height = 5
  Length = 2
  Placement = pos=(-2,-9,46) rot=(0,0,1;0rad)
  Width = 12
FEATURE [Part::Box] Box048  label="Cube046"
  Height = 5
  Length = 2
  Placement = pos=(37.5,-9,46) rot=(0,0,1;0rad)
  Width = 12
FEATURE [Part::Box] Box049  label="Cube047"
  Height = 5
  Length = 2
  Placement = pos=(8,-9,-2) rot=(0,0,1;0rad)
  Width = 12
FEATURE [Part::Box] Box050  label="Motor Mount Left001"
  Height = 16
  Length = 4
  Placement = pos=(69,-13,7) rot=(0,0,1;0rad)
  Width = 20
FEATURE [Part::Box] Box051  label="Motor Mount Right001"
  Height = 16
  Length = 4
  Placement = pos=(-46,-13,7) rot=(0,0,1;0rad)
  Width = 20
FEATURE [Part::Box] Box052  label="Motor Support Right001"
  Height = 16
  Length = 10
  Placement = pos=(-25,-1,7) rot=(0,0,1;0rad)
  Width = 8
FEATURE [Part::Box] Box053  label="Motor Support Left001"
  Height = 16
  Length = 10
  Placement = pos=(43,-1,7) rot=(0,0,1;0rad)
  Width = 8
FEATURE [Part::Box] Box054  label="Cube014 Arduino Support cube001"
  Height = 67
  Length = 55
  Placement = pos=(-13,5,-68) rot=(0,0,1;0rad)
  Width = 5
FEATURE [Part::Box] Box055  label="Cube048"
  Height = 117
  Length = 33
  Placement = pos=(-46,7,-68) rot=(0,0,1;0rad)
  Width = 3
FEATURE [Part::Box] Box056  label="Cube049"
  Height = 117
  Length = 31
  Placement = pos=(42,7,-68) rot=(0,0,1;0rad)
  Width = 3
FEATURE [Part::Cylinder] Cylinder083  label="Cylinder175"
  Angle = 360
  Height = 28
  Placement = pos=(48,20,-10) rot=(1,0,0;1.5708rad)
  Radius = 1.6
FEATURE [Part::Cylinder] Cylinder084  label="Cylinder176"
  Angle = 360
  Height = 28
  Placement = pos=(48,20,-17) rot=(1,0,0;1.5708rad)
  Radius = 1.6
FEATURE [Part::Cylinder] Cylinder085  label="Cylinder177"
  Angle = 360
  Height = 28
  Placement = pos=(55,20,-17) rot=(1,0,0;1.5708rad)
  Radius = 1.6
FEATURE [Part::Cylinder] Cylinder086  label="Cylinder178"
  Angle = 360
  Height = 28
  Placement = pos=(55,20,-10) rot=(1,0,0;1.5708rad)
  Radius = 1.6
FEATURE [Part::MultiFuse] Fusion117  label="Mount holes top left001"
  Placement = pos=(-1,0,46) rot=(0,0,1;0rad)
  Shapes = -> [Cylinder084,Cylinder085,Cylinder086,Cylinder083]
FEATURE [Part::MultiFuse] Fusion118  label="Mount holes top right001"
  Placement = pos=(-71,0,46) rot=(0,0,1;0rad)
  Shapes = -> [Cylinder084,Cylinder085,Cylinder086,Cylinder083]
FEATURE [Part::Cylinder] Cylinder087  label="Cylinder179"
  Angle = 360
  Height = 10
  Placement = pos=(0,18,29) rot=(0,0,1;0rad)
  Radius = 2.25
FEATURE [Part::Cylinder] Cylinder088  label="Cylinder180"
  Angle = 360
  Height = 10
  Placement = pos=(4.5,18,32) rot=(0,0,1;0rad)
  Radius = 1
FEATURE [Part::Cylinder] Cylinder089  label="Cylinder181"
  Angle = 360
  Height = 10
  Placement = pos=(-4.5,18,32) rot=(0,0,1;0rad)
  Radius = 1
FEATURE [Part::Fuse] Fusion119  label="Mounting Screw Holes002"
  Base = -> Cylinder088
  Tool = -> Cylinder089
FEATURE [Part::Fuse] Fusion120  label="Motor Holes Left001"
  Base = -> Cylinder087
  Placement = pos=(37,-7,-3) rot=(0.57735,0.57735,0.57735;2.0944rad)
  Tool = -> Fusion119
FEATURE [Part::Cylinder] Cylinder090  label="Cylinder182"
  Angle = 360
  Height = 10
  Placement = pos=(0,18,29) rot=(0,0,1;0rad)
  Radius = 2.25
FEATURE [Part::Cylinder] Cylinder091  label="Cylinder183"
  Angle = 360
  Height = 10
  Placement = pos=(4.5,18,32) rot=(0,0,1;0rad)
  Radius = 1
FEATURE [Part::Cylinder] Cylinder092  label="Cylinder184"
  Angle = 360
  Height = 10
  Placement = pos=(-4.5,18,32) rot=(0,0,1;0rad)
  Radius = 1
FEATURE [Part::Fuse] Fusion121  label="Mounting Screw Holes003"
  Base = -> Cylinder091
  Tool = -> Cylinder092
FEATURE [Part::Fuse] Fusion122  label="Motor Holes Right001"
  Base = -> Cylinder090
  Placement = pos=(-79,-7,-3) rot=(0.57735,0.57735,0.57735;2.0944rad)
  Tool = -> Fusion121
FEATURE [Part::Cylinder] Cylinder093  label="Cylinder185"
  Angle = 360
  Height = 28
  Placement = pos=(40.7,0,-10.3) rot=(1,0,0;1.5708rad)
  Radius = 1.6
FEATURE [Part::Cylinder] Cylinder094  label="Cylinder186"
  Angle = 360
  Height = 28
  Placement = pos=(-2.4,0,-59.8) rot=(1,0,0;1.5708rad)
  Radius = 1.6
FEATURE [Part::Cylinder] Cylinder095  label="Cylinder187"
  Angle = 360
  Height = 28
  Placement = pos=(-5,0,-9) rot=(1,0,0;1.5708rad)
  Radius = 1.6
FEATURE [Part::Cylinder] Cylinder096  label="Cylinder188"
  Angle = 360
  Height = 28
  Placement = pos=(25.5,0,-59.8) rot=(1,0,0;1.5708rad)
  Radius = 1.6
FEATURE [Part::Fuse] Fusion123
  Base = -> Cylinder094
  Tool = -> Cylinder095
FEATURE [Part::Fuse] Fusion124
  Base = -> Cylinder093
  Tool = -> Cylinder096
FEATURE [Part::Fuse] Fusion125  label="Screw holes on Arduino Duo002"
  Base = -> Fusion123
  Tool = -> Fusion124
FEATURE [Part::Mirroring] Part__Mirroring006  label="Screw holes on Arduino Duo (Mirror #1)002"
  Base = (0,0,0)
  Normal = (0,0,1)
  Placement = pos=(-4,10,-67) rot=(0,0,1;0rad)
  Source = -> Fusion125
FEATURE [Part::Mirroring] Part__Mirroring007  label="Screw holes on Arduino Duo (Mirror #1)001 (Mirror #4)001"
  Base = (0,0,0)
  Normal = (1,0,0)
  Placement = pos=(27,0,-6) rot=(0,0,1;0rad)
  Source = -> Part__Mirroring006
FEATURE [Part::Box] Box057  label="Cube050"
  Height = 50
  Length = 47
  Placement = pos=(-9,-8,0) rot=(0,0,1;0rad)
  Width = 12
FEATURE [Part::Box] Box058  label="Cube051"
  Height = 55
  Length = 53
  Placement = pos=(-12,-8,-2.5) rot=(0,0,1;0rad)
  Width = 11
FEATURE [Part::Cut] Cut045029
  Base = -> Box058
  Tool = -> Box057
FEATURE [Part::Box] Box059  label="Cube052"
  Height = 5
  Length = 3
  Placement = pos=(35,-9,-4) rot=(0,0,1;0rad)
  Width = 12
FEATURE [Part::Cut] Cut045030
  Base = -> Cut045029
  Placement = pos=(-9,10,-58) rot=(1,0,0;1.5708rad)
  Tool = -> Box059
FEATURE [Part::Cut] Cut045031
  Base = -> Cut045029
  Placement = pos=(36.7,10,-56.7) rot=(1,0,0;1.5708rad)
  Tool = -> Box059
FEATURE [Part::Cut] Cut045032
  Base = -> Cut045029
  Placement = pos=(-6.4,10,-7.2) rot=(1,0,0;1.5708rad)
  Tool = -> Box059
FEATURE [Part::Cut] Cut045033
  Base = -> Cut045029
  Placement = pos=(21.5,10,-7.2) rot=(1,0,0;1.5708rad)
  Tool = -> Box059
FEATURE [Part::MultiFuse] Fusion126
  Shapes = -> [Cut045030,Cut045033,Cut045031,Cut045032]
FEATURE [Part::Mirroring] Part__Mirroring008  label="Hex Holes001"
  Base = (0,0,0)
  Normal = (1,0,0)
  Placement = pos=(27,0,-6) rot=(0,0,1;0rad)
  Source = -> Fusion126
FEATURE [Part::Box] Box060  label="Cube053"
  Height = 5
  Length = 2
  Placement = pos=(37.5,-9,-2) rot=(0,0,1;0rad)
  Width = 12
FEATURE [Part::Box] Box061  label="Battery Base001"
  Height = 50
  Length = 55
  Placement = pos=(-13,3,-1) rot=(0,0,1;0rad)
  Width = 7
FEATURE [Part::Cylinder] Cylinder097  label="Cylinder189"
  Angle = 360
  Height = 42
  Radius = 4.8
FEATURE [Part::Cylinder] Cylinder098  label="Cylinder190"
  Angle = 360
  Height = 1.6
  Placement = pos=(0,0,42) rot=(0,0,1;0rad)
  Radius = 1.65
FEATURE [Part::Fuse] Fusion127
  Base = -> Cylinder097
  Placement = pos=(2,0,0) rot=(0,0,1;0rad)
  Tool = -> Cylinder098
FEATURE [Part::Cylinder] Cylinder099  label="Cylinder191"
  Angle = 360
  Height = 42
  Radius = 4.8
FEATURE [Part::Cylinder] Cylinder100  label="Cylinder192"
  Angle = 360
  Height = 1.6
  Placement = pos=(0,0,42) rot=(0,0,1;0rad)
  Radius = 1.65
FEATURE [Part::Fuse] Fusion128
  Base = -> Cylinder099
  Placement = pos=(12,0,0) rot=(0,0,1;0rad)
  Tool = -> Cylinder100
FEATURE [Part::Cylinder] Cylinder101  label="Cylinder193"
  Angle = 360
  Height = 42
  Radius = 4.8
FEATURE [Part::Cylinder] Cylinder102  label="Cylinder194"
  Angle = 360
  Height = 1.6
  Placement = pos=(0,0,42) rot=(0,0,1;0rad)
  Radius = 1.65
FEATURE [Part::Fuse] Fusion129
  Base = -> Cylinder101
  Placement = pos=(22,0,0) rot=(0,0,1;0rad)
  Tool = -> Cylinder102
FEATURE [Part::Cylinder] Cylinder103  label="Cylinder195"
  Angle = 360
  Height = 42
  Radius = 4.8
FEATURE [Part::Cylinder] Cylinder104  label="Cylinder196"
  Angle = 360
  Height = 1.6
  Placement = pos=(0,0,42) rot=(0,0,1;0rad)
  Radius = 1.65
FEATURE [Part::Fuse] Fusion130
  Base = -> Cylinder103
  Placement = pos=(32,0,0) rot=(0,0,1;0rad)
  Tool = -> Cylinder104
FEATURE [Part::Cylinder] Cylinder105  label="Cylinder197"
  Angle = 360
  Height = 42
  Radius = 4.8
FEATURE [Part::Cylinder] Cylinder106  label="Cylinder198"
  Angle = 360
  Height = 1.6
  Placement = pos=(0,0,42) rot=(0,0,1;0rad)
  Radius = 1.65
FEATURE [Part::Fuse] Fusion131
  Base = -> Cylinder105
  Placement = pos=(-8,0,0) rot=(0,0,1;0rad)
  Tool = -> Cylinder106
FEATURE [Part::MultiFuse] Fusion132  label="AAA Batts002"
  Placement = pos=(2,0,2) rot=(0,0,1;0rad)
  Shapes = -> [Fusion131,Fusion127,Fusion128,Fusion129,Fusion130]
FEATURE [Part::Cut] Cut045034
  Base = -> Box061
  Tool = -> Fusion132
FEATURE [Part::Box] Box062  label="Cube054"
  Height = 2.5
  Length = 55
  Placement = pos=(-13,-9,-1) rot=(0,0,1;0rad)
  Width = 12
FEATURE [Part::Box] Box063  label="Cube055"
  Height = 2.5
  Length = 55
  Placement = pos=(-13,-9,46.5) rot=(0,0,1;0rad)
  Width = 12
FEATURE [Part::Box] Box064  label="Cube056"
  Height = 50
  Length = 2.5
  Placement = pos=(-13,-9,-1) rot=(0,0,1;0rad)
  Width = 12
FEATURE [Part::Box] Box065  label="Cube057"
  Height = 50
  Length = 2.5
  Placement = pos=(39.5,-9,-1) rot=(0,0,1;0rad)
  Width = 12
FEATURE [Part::MultiFuse] Fusion133
  Shapes = -> [Box062,Box064,Box065,Box063]
FEATURE [Part::Box] Box066  label="Cube058"
  Height = 5
  Length = 2
  Placement = pos=(-10.5,-9,46) rot=(0,0,1;0rad)
  Width = 12
FEATURE [Part::Box] Box067  label="Cube059"
  Height = 5
  Length = 2
  Placement = pos=(-10.5,-9,-2) rot=(0,0,1;0rad)
  Width = 12
FEATURE [Part::MultiFuse] Fusion134
  Shapes = -> [Box067,Box066,Box060,Box048]
FEATURE [Part::MultiFuse] Fusion135
  Shapes = -> [Box045,Box046,Box047,Box049]
FEATURE [Part::Cut] Cut045035
  Base = -> Fusion133
  Tool = -> Fusion134
FEATURE [Part::Cut] Cut045036
  Base = -> Cut045035
  Tool = -> Fusion135
FEATURE [Part::Cylinder] Cylinder107  label="Cylinder199"
  Angle = 360
  Height = 14.5
  Placement = pos=(-43.6,-2.4,-15) rot=(0,0,1;0rad)
  Radius = 0.8
FEATURE [Part::Cylinder] Cylinder108  label="Cylinder200"
  Angle = 360
  Height = 14.5
  Placement = pos=(-43.6,-13.8,-15) rot=(0,0,1;0rad)
  Radius = 0.8
FEATURE [Part::Fuse] Fusion136
  Base = -> Cut045034
  Tool = -> Cut045036
FEATURE [Part::Box] Box068  label="Cube060"
  Height = 4
  Length = 12
  Placement = pos=(-50,-16.75,-14) rot=(0,0,1;0rad)
  Width = 26.75
FEATURE [Part::Chamfer] Chamfer002
  Base = -> Box068
  Edges = 1 edges r=7: [Edge3]
FEATURE [Part::Cone] Cone004
  Angle = 360
  Height = 1.5
  Placement = pos=(-43.6,-2.4,-10) rot=(0,0,1;0rad)
  Radius1 = 2.75
  Radius2 = 1.25
FEATURE [Part::Cone] Cone005
  Angle = 360
  Height = 1.5
  Placement = pos=(-43.6,-13.8,-10) rot=(0,0,1;0rad)
  Radius1 = 2.75
  Radius2 = 1.25
FEATURE [Part::Fuse] Fusion137
  Base = -> Cone004
  Tool = -> Cone005
FEATURE [Part::Fuse] Fusion138
  Base = -> Chamfer002
  Tool = -> Fusion137
FEATURE [Part::Fuse] Fusion139
  Base = -> Cylinder107
  Tool = -> Cylinder108
FEATURE [Part::Cut] Cut045037
  Base = -> Fusion138
  Tool = -> Fusion139
FEATURE [Part::Cylinder] Cylinder109  label="Cylinder201"
  Angle = 360
  Height = 14.5
  Placement = pos=(-43.6,-2.4,-15) rot=(0,0,1;0rad)
  Radius = 0.8
FEATURE [Part::Cylinder] Cylinder110  label="Cylinder202"
  Angle = 360
  Height = 14.5
  Placement = pos=(-43.6,-13.8,-15) rot=(0,0,1;0rad)
  Radius = 0.8
FEATURE [Part::Box] Box069  label="Cube061"
  Height = 4
  Length = 12
  Placement = pos=(-50,-16.75,-14) rot=(0,0,1;0rad)
  Width = 26.75
FEATURE [Part::Chamfer] Chamfer003
  Base = -> Box069
  Edges = 1 edges r=7: [Edge3]
FEATURE [Part::Cone] Cone006
  Angle = 360
  Height = 1.5
  Placement = pos=(-43.6,-2.4,-10) rot=(0,0,1;0rad)
  Radius1 = 2.75
  Radius2 = 1.25
FEATURE [Part::Cone] Cone007
  Angle = 360
  Height = 1.5
  Placement = pos=(-43.6,-13.8,-10) rot=(0,0,1;0rad)
  Radius1 = 2.75
  Radius2 = 1.25
FEATURE [Part::Fuse] Fusion140
  Base = -> Cone006
  Tool = -> Cone007
FEATURE [Part::Fuse] Fusion141
  Base = -> Chamfer003
  Tool = -> Fusion140
FEATURE [Part::Fuse] Fusion142
  Base = -> Cylinder109
  Tool = -> Cylinder110
FEATURE [Part::Cut] Cut045038
  Base = -> Fusion141
  Tool = -> Fusion142
FEATURE [Part::Mirroring] Part__Mirroring009  label="Cut045028 (Mirror #6)001"
  Base = (0,0,0)
  Normal = (1,0,0)
  Placement = pos=(27,0,0) rot=(0,0,1;0rad)
  Source = -> Cut045038
FEATURE [Part::Cut] Cut045039
  Base = -> Box050
  Tool = -> Fusion120
FEATURE [Part::Cut] Cut045040
  Base = -> Box051
  Tool = -> Fusion122
FEATURE [Part::MultiFuse] Fusion143
  Shapes = -> [Box054,Box055,Box056]
FEATURE [Part::Fuse] Fusion144
  Base = -> Fusion136
  Tool = -> Fusion143
FEATURE [Part::MultiFuse] Fusion145
  Shapes = -> [Fusion144,Cut045040,Cut045039]
FEATURE [Part::MultiFuse] Fusion146
  Shapes = -> [Fusion145,Part__Mirroring009,Cut045037]
FEATURE [Part::Cut] Cut045041
  Base = -> Fusion146
  Tool = -> Fusion117
FEATURE [Part::Cut] Cut045042
  Base = -> Cut045041
  Tool = -> Fusion118
FEATURE [Part::Cut] Cut045043
  Base = -> Cut045042
  Tool = -> Part__Mirroring007
FEATURE [Part::Cut] Cut045044
  Base = -> Cut045043
  Tool = -> Part__Mirroring008
FEATURE [Part::MultiFuse] Fusion147
  Shapes = -> [Cut045044,Box053,Box052]
FEATURE [Part::Chamfer] Chamfer004
  Base = -> Fusion147
  Edges = 1 edges r=25: [Edge43]
FEATURE [Part::Chamfer] Chamfer005
  Base = -> Chamfer004
  Edges = 1 edges r=25: [Edge225]
FEATURE [Part::Chamfer] Chamfer006
  Base = -> Chamfer005
  Edges = 1 edges r=30: [Edge58]
FEATURE [Part::Chamfer] Chamfer007
  Base = -> Chamfer006
  Edges = 1 edges r=30: [Edge148]
FEATURE [Part::Fillet] Fillet
  Base = -> Chamfer007
  Edges = 1 edges r=2: [Edge233]
FEATURE [Part::Fillet] Fillet001
  Base = -> Fillet
  Edges = 1 edges r=2: [Edge6]
FEATURE [Part::Fillet] Fillet002
  Base = -> Fillet001
  Edges = 1 edges r=2: [Edge2]
FEATURE [Part::Fillet] Fillet003
  Base = -> Fillet002
  Edges = 1 edges r=2: [Edge357]
FEATURE [Part::Fillet] Fillet004
  Base = -> Fillet003
  Edges = 1 edges r=2: [Edge6]
FEATURE [Part::Fillet] Fillet005
  Base = -> Fillet004
  Edges = 1 edges r=2: [Edge2]
FEATURE [Part::Fillet] Fillet006
  Base = -> Fillet005
  Edges = 1 edges r=2: [Edge407]
FEATURE [Part::Fillet] Fillet007
  Base = -> Fillet006
  Edges = 1 edges r=2: [Edge2]
FEATURE [Part::Fillet] Fillet008
  Base = -> Fillet007
  Edges = 1 edges r=2: [Edge369]
FEATURE [Part::Fillet] Fillet009
  Base = -> Fillet008
  Edges = 1 edges r=2: [Edge2]
FEATURE [Part::Cylinder] Cylinder111  label="Cylinder203"
  Angle = 360
  Height = 28
  Placement = pos=(45,6,47) rot=(0.707107,0,0.707107;4.01426rad)
  Radius = 0.5
FEATURE [Part::Cylinder] Cylinder112  label="Cylinder204"
  Angle = 360
  Height = 28
  Placement = pos=(66,6,26) rot=(0.707107,0,0.707107;4.01426rad)
  Radius = 0.5
FEATURE [Part::Cut] Cut045045
  Base = -> Fillet009
  Tool = -> Cylinder111
FEATURE [Part::Cut] Cut045046
  Base = -> Cut045045
  Tool = -> Cylinder112
FEATURE [Part::Cylinder] Cylinder113  label="Cylinder205"
  Angle = 360
  Height = 28
  Placement = pos=(66,6,26) rot=(0.707107,0,0.707107;4.01426rad)
  Radius = 0.5
FEATURE [Part::Mirroring] Part__Mirroring010  label="Cylinder137 (Mirror #7)"
  Base = (0,0,0)
  Normal = (1,0,0)
  Placement = pos=(27,0,0) rot=(0,0,1;0rad)
  Source = -> Cylinder113
FEATURE [Part::Cylinder] Cylinder114  label="Cylinder206"
  Angle = 360
  Height = 28
  Placement = pos=(45,6,47) rot=(0.707107,0,0.707107;4.01426rad)
  Radius = 0.5
FEATURE [Part::Mirroring] Part__Mirroring011  label="Cylinder138 (Mirror #8)"
  Base = (0,0,0)
  Normal = (1,0,0)
  Placement = pos=(27,0,0) rot=(0,0,1;0rad)
  Source = -> Cylinder114
FEATURE [Part::Cut] Cut045047
  Base = -> Cut045046
  Tool = -> Part__Mirroring010
FEATURE [Part::Cut] Cut045048
  Base = -> Cut045047
  Tool = -> Part__Mirroring011
FEATURE [Part::Cylinder] Cylinder115  label="Arduino Cylinder191"
  Angle = 360
  Height = 28
  Placement = pos=(4,11,-8.6) rot=(1,0,0;1.5708rad)
  Radius = 1.6
FEATURE [Part::Cylinder] Cylinder116  label="Arduino Cylinder192"
  Angle = 360
  Height = 28
  Placement = pos=(31.9,11,-8.6) rot=(1,0,0;1.5708rad)
  Radius = 1.6
FEATURE [Part::Cylinder] Cylinder117  label="Arduino Cylinder193"
  Angle = 360
  Height = 28
  Placement = pos=(-11.2,11,-59.4) rot=(1,0,0;1.5708rad)
  Radius = 1.6
FEATURE [Part::Cylinder] Cylinder118  label="Arduino Cylinder194"
  Angle = 360
  Height = 28
  Placement = pos=(37,11,-60.7) rot=(1,0,0;1.5708rad)
  Radius = 1.6
FEATURE [Part::Cylinder] Cylinder119  label="Arduino Cylinder195"
  Angle = 360
  Height = 2.5
  Placement = pos=(4,13,-8.6) rot=(1,0,0;1.5708rad)
  Radius = 4
FEATURE [Part::Feature] Box014001
  Placement = pos=(3.88157,4,-2.89487) rot=(0,1,0;1.0472rad)
  shape: bbox 13.66 x 10 x 13.66 mm, 6 faces (baked)
FEATURE [Part::Feature] Box014002
  Placement = pos=(8.88157,4,-5.64487) rot=(0,1,0;2.0944rad)
  shape: bbox 13.66 x 10 x 13.66 mm, 6 faces (baked)
FEATURE [Part::Feature] Box014003
  Placement = pos=(9,4,-11.35) rot=(0,1,0;3.14159rad)
  shape: bbox 10 x 10 x 10 mm, 6 faces (baked)
FEATURE [Part::Feature] Box014004
  Placement = pos=(4.11843,4,-14.3051) rot=(0,1,0;4.18879rad)
  shape: bbox 13.66 x 10 x 13.66 mm, 6 faces (baked)
FEATURE [Part::Feature] Box014005
  Placement = pos=(-0.88157,4,-11.5551) rot=(0,-1,0;1.0472rad)
  shape: bbox 13.66 x 10 x 13.66 mm, 6 faces (baked)
FEATURE [Part::MultiFuse] Fusion148
  Shapes = -> [Box014001,Box014002,Box014004,Box014003,Box014005,Box014]
FEATURE [Part::Cut] Cut045049  label="M3 Nut004"
  Base = -> Cylinder119
  Placement = pos=(0,-3,0) rot=(0,0,1;0rad)
  Tool = -> Fusion148
FEATURE [Part::Box] Box014006  label="Not used Cube001"
  Height = 10
  Length = 10
  Placement = pos=(-1,4,-5.85) rot=(0,0,1;0rad)
  Width = 10
FEATURE [Part::Cylinder] Cylinder120  label="Arduino Cylinder196"
  Angle = 360
  Height = 2.5
  Placement = pos=(4,13,-8.6) rot=(1,0,0;1.5708rad)
  Radius = 4
FEATURE [Part::Feature] Box014007
  Placement = pos=(3.88157,4,-2.89487) rot=(0,1,0;1.0472rad)
  shape: bbox 13.66 x 10 x 13.66 mm, 6 faces (baked)
FEATURE [Part::Feature] Box014008
  Placement = pos=(8.88157,4,-5.64487) rot=(0,1,0;2.0944rad)
  shape: bbox 13.66 x 10 x 13.66 mm, 6 faces (baked)
FEATURE [Part::Feature] Box014009
  Placement = pos=(9,4,-11.35) rot=(0,1,0;3.14159rad)
  shape: bbox 10 x 10 x 10 mm, 6 faces (baked)
FEATURE [Part::Feature] Box014010
  Placement = pos=(4.11843,4,-14.3051) rot=(0,1,0;4.18879rad)
  shape: bbox 13.66 x 10 x 13.66 mm, 6 faces (baked)
FEATURE [Part::Feature] Box014011
  Placement = pos=(-0.88157,4,-11.5551) rot=(0,-1,0;1.0472rad)
  shape: bbox 13.66 x 10 x 13.66 mm, 6 faces (baked)
FEATURE [Part::MultiFuse] Fusion149
  Shapes = -> [Box014007,Box014008,Box014010,Box014009,Box014011,Box014006]
FEATURE [Part::Cut] Cut045050  label="M3 Nut005"
  Base = -> Cylinder120
  Placement = pos=(27.9,-3,0) rot=(0,0,1;0rad)
  Tool = -> Fusion149
FEATURE [Part::Box] Box014012  label="Not used Cube002"
  Height = 10
  Length = 10
  Placement = pos=(-1,4,-5.85) rot=(0,0,1;0rad)
  Width = 10
FEATURE [Part::Cylinder] Cylinder121  label="Arduino Cylinder197"
  Angle = 360
  Height = 2.5
  Placement = pos=(4,13,-8.6) rot=(1,0,0;1.5708rad)
  Radius = 4
FEATURE [Part::Feature] Box014013
  Placement = pos=(3.88157,4,-2.89487) rot=(0,1,0;1.0472rad)
  shape: bbox 13.66 x 10 x 13.66 mm, 6 faces (baked)
FEATURE [Part::Feature] Box014014
  Placement = pos=(8.88157,4,-5.64487) rot=(0,1,0;2.0944rad)
  shape: bbox 13.66 x 10 x 13.66 mm, 6 faces (baked)
FEATURE [Part::Feature] Box014015
  Placement = pos=(9,4,-11.35) rot=(0,1,0;3.14159rad)
  shape: bbox 10 x 10 x 10 mm, 6 faces (baked)
FEATURE [Part::Feature] Box014016
  Placement = pos=(4.11843,4,-14.3051) rot=(0,1,0;4.18879rad)
  shape: bbox 13.66 x 10 x 13.66 mm, 6 faces (baked)
FEATURE [Part::Feature] Box014017
  Placement = pos=(-0.88157,4,-11.5551) rot=(0,-1,0;1.0472rad)
  shape: bbox 13.66 x 10 x 13.66 mm, 6 faces (baked)
FEATURE [Part::MultiFuse] Fusion150
  Shapes = -> [Box014013,Box014014,Box014016,Box014015,Box014017,Box014012]
FEATURE [Part::Cut] Cut045051  label="M3 Nut006"
  Base = -> Cylinder121
  Placement = pos=(-15.2,-3,-50.8) rot=(0,0,1;0rad)
  Tool = -> Fusion150
FEATURE [Part::Box] Box014018  label="Not used Cube003"
  Height = 10
  Length = 10
  Placement = pos=(-1,4,-5.85) rot=(0,0,1;0rad)
  Width = 10
FEATURE [Part::Cylinder] Cylinder122  label="Arduino Cylinder198"
  Angle = 360
  Height = 2.5
  Placement = pos=(4,13,-8.6) rot=(1,0,0;1.5708rad)
  Radius = 4
FEATURE [Part::Feature] Box014019
  Placement = pos=(3.88157,4,-2.89487) rot=(0,1,0;1.0472rad)
  shape: bbox 13.66 x 10 x 13.66 mm, 6 faces (baked)
FEATURE [Part::Feature] Box014020
  Placement = pos=(8.88157,4,-5.64487) rot=(0,1,0;2.0944rad)
  shape: bbox 13.66 x 10 x 13.66 mm, 6 faces (baked)
FEATURE [Part::Feature] Box014021
  Placement = pos=(9,4,-11.35) rot=(0,1,0;3.14159rad)
  shape: bbox 10 x 10 x 10 mm, 6 faces (baked)
FEATURE [Part::Feature] Box014022
  Placement = pos=(4.11843,4,-14.3051) rot=(0,1,0;4.18879rad)
  shape: bbox 13.66 x 10 x 13.66 mm, 6 faces (baked)
FEATURE [Part::Feature] Box014023
  Placement = pos=(-0.88157,4,-11.5551) rot=(0,-1,0;1.0472rad)
  shape: bbox 13.66 x 10 x 13.66 mm, 6 faces (baked)
FEATURE [Part::MultiFuse] Fusion151
  Shapes = -> [Box014019,Box014020,Box014022,Box014021,Box014023,Box014018]
FEATURE [Part::Cut] Cut045052  label="M3 Nut007"
  Base = -> Cylinder122
  Placement = pos=(33,-3,-52.1) rot=(0,0,1;0rad)
  Tool = -> Fusion151
FEATURE [Part::Box] Box014024  label="Cube062"
  Height = 67
  Length = 65
  Placement = pos=(-16,-13,-6) rot=(0,0,1;0rad)
  Width = 8
FEATURE [Part::Cut] Cut045053  label="BAtt Holder"
  Base = -> Fusion110
  Tool = -> Box014024
FEATURE [Part::Cylinder] Cylinder123  label="Cylinder209"
  Angle = 360
  Height = 28
  Placement = pos=(45,6,47) rot=(0.707107,0,0.707107;4.01426rad)
  Radius = 0.5
FEATURE [Part::Cylinder] Cylinder124  label="Cylinder210"
  Angle = 360
  Height = 28
  Placement = pos=(66,6,26) rot=(0.707107,0,0.707107;4.01426rad)
  Radius = 0.5
FEATURE [Part::Cylinder] Cylinder125  label="Cylinder211"
  Angle = 360
  Height = 28
  Placement = pos=(45,6,47) rot=(0.707107,0,0.707107;4.01426rad)
  Radius = 0.5
FEATURE [Part::Cylinder] Cylinder126  label="Cylinder212"
  Angle = 360
  Height = 28
  Placement = pos=(66,6,26) rot=(0.707107,0,0.707107;4.01426rad)
  Radius = 0.5
FEATURE [Part::Mirroring] Part__Mirroring012  label="Cylinder211 (Mirror #13)"
  Base = (0,0,0)
  Normal = (1,0,0)
  Placement = pos=(27,0,0) rot=(0,0,1;0rad)
  Source = -> Cylinder125
FEATURE [Part::Mirroring] Part__Mirroring013  label="Cylinder212 (Mirror #14)"
  Base = (0,0,0)
  Normal = (1,0,0)
  Placement = pos=(27,0,0) rot=(0,0,1;0rad)
  Source = -> Cylinder126
